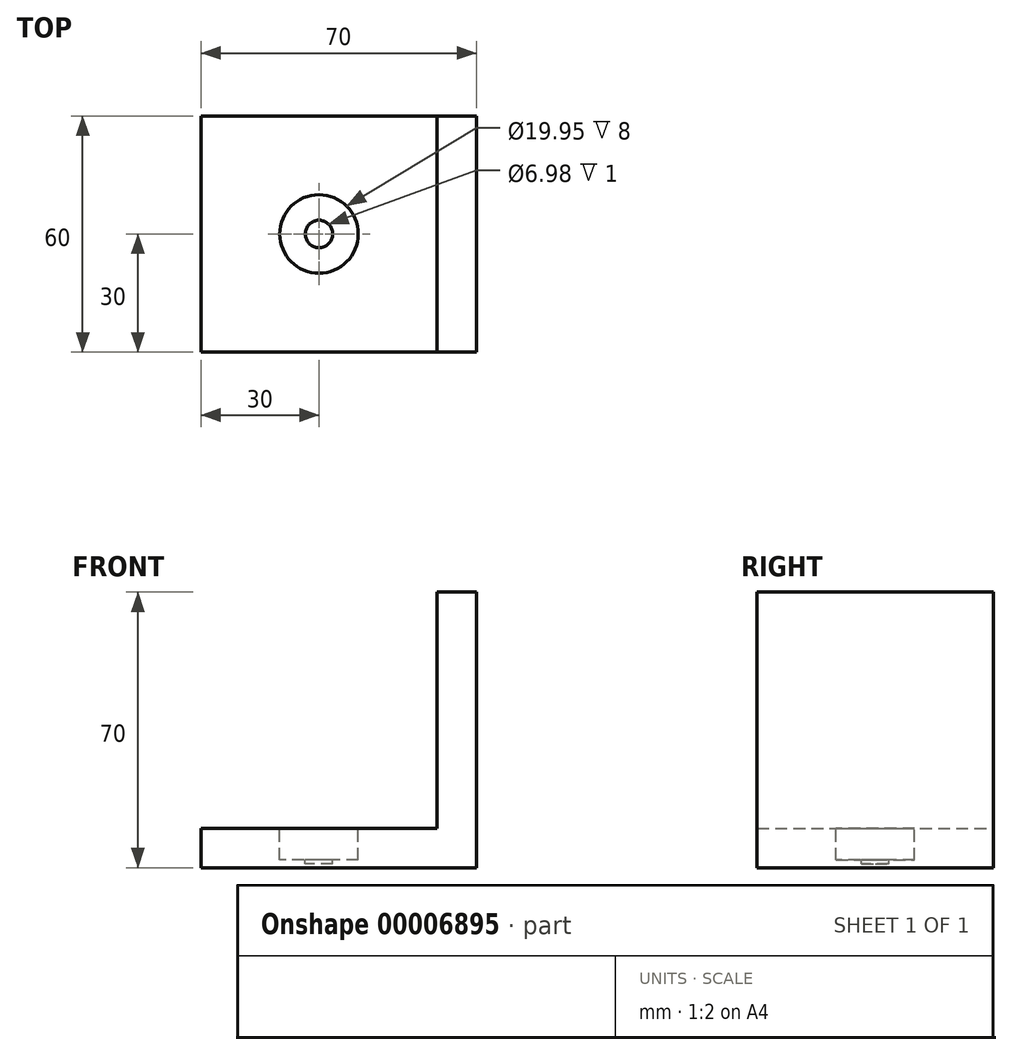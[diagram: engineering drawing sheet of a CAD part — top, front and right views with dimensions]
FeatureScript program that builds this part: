
annotation { "Feature Type Name" : "Feature", "Feature Type Description" : "" }
export const myFeature = defineFeature(function(context is Context, id is Id, definition is map)
    precondition{}
    {
        {
            var Q0;
            Q0=qCreatedBy(makeId("Top.planeOp"),FACE);
            var sketch = newSketch(context, id + "F0", { "sketchPlane" : qUnion([Q0])});
            skLineSegment(sketch, "E0.rect.bottom", {"start": v(35, -30) * mm, "end": v(-35, -30) * mm});
            skLineSegment(sketch, "E0.rect.top", {"start": v(35, 30) * mm, "end": v(-35, 30) * mm});
            skLineSegment(sketch, "E0.rect.left", {"start": v(35, -30) * mm, "end": v(35, 30) * mm});
            skLineSegment(sketch, "E0.rect.right", {"start": v(-35, -30) * mm, "end": v(-35, 30) * mm});
            skPoint(sketch, "E0.rect.middle", {"position": v(0, 0) * mm});
            skLineSegment(sketch, "E1", {"start": v(25, 30) * mm, "end": v(25, -30) * mm});
            skSolve(sketch);
        }
        {
            var Q0;
            {var subQ1=sQuery(id+"F0.wireOp",EDGE,"E0.rect.left");Q0=makeQuery(id+"F0.imprint","IMPRINT",FACE,{"disambiguationData":[TD([[makeQuery(id+"F0.imprint","IMPRINT",EDGE,{"derivedFrom":subQ1}),1.0]])]});}
            var Q1;
            {var subQ1=sQuery(id+"F0.wireOp",EDGE,"E0.rect.right");Q1=makeQuery(id+"F0.imprint","IMPRINT",FACE,{"disambiguationData":[TD([[makeQuery(id+"F0.imprint","IMPRINT",EDGE,{"derivedFrom":subQ1}),-1.0]])]});}
            extrude(context, id + "F1", {"entities" : qUnion([Q0, Q1]), "depth" : 10 * mm});
        }
        {
            var Q0;
            Q0=makeQuery(id+"F1.opExtrude","CAP_FACE",FACE,{"disambiguationData":[OSD([sQuery(id+"F0.wireOp",EDGE,"E0.rect.bottom"),sQuery(id+"F0.wireOp",EDGE,"E0.rect.top"),sQuery(id+"F0.wireOp",EDGE,"E0.rect.left"),sQuery(id+"F0.wireOp",EDGE,"E0.rect.right")])],"isStart":false});
            var sketch = newSketch(context, id + "F2", { "sketchPlane" : qUnion([Q0])});
            skLineSegment(sketch, "E2", {"start": v(25, 30) * mm, "end": v(25, -30) * mm});
            skSolve(sketch);
        }
        {
            var Q0;
            Q0=qSketchRegion(id+"F2",true);
            var Q1;
            {var subQ1=sQuery(id+"F2.wireOp",EDGE,"E2");Q1=makeQuery(id+"F2.imprint","IMPRINT",FACE,{"disambiguationData":[TD([[makeQuery(id+"F2.imprint","IMPRINT",EDGE,{"derivedFrom":subQ1}),1.0]])]});}
            extrude(context, id + "F3", {"entities" : qUnion([Q0, Q1]), "operationType" : NewBodyOperationType.ADD, "depth" : 60 * mm});
        }
        {
            var Q0;
            Q0=makeQuery(id+"F1.opExtrude","CAP_FACE",FACE,{"disambiguationData":[OSD([sQuery(id+"F0.wireOp",EDGE,"E0.rect.bottom"),sQuery(id+"F0.wireOp",EDGE,"E0.rect.top"),sQuery(id+"F0.wireOp",EDGE,"E0.rect.left"),sQuery(id+"F0.wireOp",EDGE,"E0.rect.right")])],"isStart":false});
            var sketch = newSketch(context, id + "F4", { "sketchPlane" : qUnion([Q0])});
            skLineSegment(sketch, "E3", {"start": v(-5, 30) * mm, "end": v(-5, -30) * mm, "construction": true});
            skLineSegment(sketch, "E4", {"start": v(25, 0) * mm, "end": v(-35, 0) * mm, "construction": true});
            skCircle(sketch, "E5", {"center": v(-5, 0) * mm, "radius": 9.98 * mm});
            skSolve(sketch);
        }
        {
            var Q0;
            Q0=makeQuery(id+"F4.imprint","IMPRINT",FACE,{"disambiguationData":[TD([[makeQuery(id+"F4.imprint","IMPRINT",EDGE,{"derivedFrom":sQuery(id+"F4.wireOp",EDGE,"E5")}),1.0]])]});
            var Q1;
            Q1=makeQuery(id+"F4.imprint","IMPRINT",FACE,{"disambiguationData":[TD([[makeQuery(id+"F4.imprint","IMPRINT",EDGE,{"derivedFrom":sQuery(id+"F4.wireOp",EDGE,"03ee1e25-1de1-4310-ad50-a49f000c9076")}),1.0]])]});
            var Q2;
            Q2=makeQuery(id+"F4.imprint","IMPRINT",FACE,{"disambiguationData":[TD([[makeQuery(id+"F4.imprint","IMPRINT",EDGE,{"derivedFrom":sQuery(id+"F4.wireOp",EDGE,"84919f80-77ee-42fb-8425-d8fb0a051967")}),1.0]])]});
            var Q3;
            Q3=makeQuery(id+"F4.imprint","IMPRINT",FACE,{"disambiguationData":[TD([[makeQuery(id+"F4.imprint","IMPRINT",EDGE,{"derivedFrom":sQuery(id+"F4.wireOp",EDGE,"66c9013f-d209-4984-8236-24a5fc568936")}),1.0]])]});
            var Q4;
            Q4=makeQuery(id+"F4.imprint","IMPRINT",FACE,{"disambiguationData":[TD([[makeQuery(id+"F4.imprint","IMPRINT",EDGE,{"derivedFrom":sQuery(id+"F4.wireOp",EDGE,"4cb79e47-d396-4294-a89a-cb36e9a160a2")}),1.0]])]});
            var Q5;
            Q5=makeQuery(id+"F4.imprint","IMPRINT",FACE,{"disambiguationData":[TD([[makeQuery(id+"F4.imprint","IMPRINT",EDGE,{"derivedFrom":sQuery(id+"F4.wireOp",EDGE,"e0911776-ae68-4c96-acfb-ec6cdf3edbad")}),1.0]])]});
            var Q6;
            Q6=makeQuery(id+"F4.imprint","IMPRINT",FACE,{"disambiguationData":[TD([[makeQuery(id+"F4.imprint","IMPRINT",EDGE,{"derivedFrom":sQuery(id+"F4.wireOp",EDGE,"5f179750-4f3a-4309-9aa9-b5c8024dfe7b")}),1.0]])]});
            extrude(context, id + "F5", {"entities" : qUnion([Q0, Q1, Q2, Q3, Q4, Q5, Q6]), "operationType" : NewBodyOperationType.REMOVE, "oppositeDirection" : true, "depth" : 8 * mm});
        }
        {
            var Q0;
            Q0=makeQuery(id+"F5.boolean.opBoolean","COPY",FACE,{"derivedFrom":makeQuery(id+"F5.opExtrude","CAP_FACE",FACE,{"disambiguationData":[OSD([sQuery(id+"F4.wireOp",EDGE,"E5")])],"isStart":false})});
            var sketch = newSketch(context, id + "F6", { "sketchPlane" : qUnion([Q0])});
            skCircle(sketch, "E6", {"center": v(-5, 0) * mm, "radius": 3.49 * mm});
            skSolve(sketch);
        }
        {
            var Q0;
            Q0=makeQuery(id+"F6.imprint","IMPRINT",FACE,{"disambiguationData":[TD([[makeQuery(id+"F6.imprint","IMPRINT",EDGE,{"derivedFrom":sQuery(id+"F6.wireOp",EDGE,"E6")}),1.0]])]});
            extrude(context, id + "F7", {"entities" : qUnion([Q0]), "operationType" : NewBodyOperationType.REMOVE, "oppositeDirection" : true, "depth" : 1 * mm});
        }
    });
